# Revit family: 1Doors_Mincey-Marble-Manufacturing_Napoli-Reverse
name_source: partatom
category: Doors
units: mm (PartAtom-declared; Revit-internal decimal feet)

## family parameters
Always vertical = Yes
Cut with Voids When Loaded = No
OmniClass Number = 23.45.05.14.11.24
Room Calculation Point = No
Shared = No
Work Plane-Based = Yes

## types (1)
- NAPSDR - 60 X 76 - Polished/Brushed - Clear
    Default Elevation = 48 "
    Description = Reversed Napoli Sliding Barn Shower Doors, frameless shower door, tempered glass, customizable
    Door Width = 30 "
    Fixed Panel = 32 "
    Glass Material = Mincey Marble Manufacturing - Glass - Clear
    Glass Material Note = Available glass type: Clear, Frosted
    Glass Thickness = 0 "
    Height = 76 "
    Height Limits = 76 "
    Height Note = Available custom sizes. Please, contact the manufacturer.
    Manufacturer = Mincey Marble Manufacturing
    Model = NAPSDR - 60 X 76 - Polished/Brushed - Clear
    Product Documentation Link = https://minceymarble.com
    Product Material = Mincey Marble Manufacturing - Metal - Polished
    Product Material Note = Available finishes: Polished, Brushed, Black Matte
    Product Page URL = https://minceymarble.com
    Rough Height = 76 "
    Rough Width = 60 "
    Sliding Panel 1 = 30 "
    Thickness = 3 "
    URL = https://minceymarble.com
    Version = 1
    Width = 60 "
    Width Limits = 60 "
    Width Note = Available custom sizes. Please, contact the manufacturer.

## geometry (parser evidence)
native form markers: Sweep x2
no freeform markers — native parametric forms only
